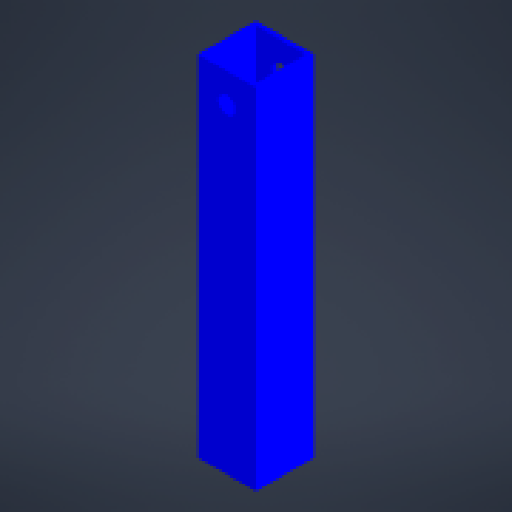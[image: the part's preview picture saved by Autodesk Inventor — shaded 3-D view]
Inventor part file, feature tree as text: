
AUTODESK INVENTOR PART (.ipt)
format: ipt  version: 2024 (Build 280153000, 153)  size: 149,504 bytes
history: native  units: mm
features: extrude x2, sketch x2, other x1
ambient origin geometry x8: Origin, YZ Plane, XZ Plane, XY Plane, X Axis, Y Axis, Z Axis, Center Point
bodies: Body1 (feature_tree)
feature tree (5):
  other  "Твердое тело1"
  extrude  "Выдавливание1"  Depth=1.5mm
  extrude  "Выдавливание2"  Depth=20.0mm
  sketch  "Эскиз1"
  sketch  "Эскиз2"
